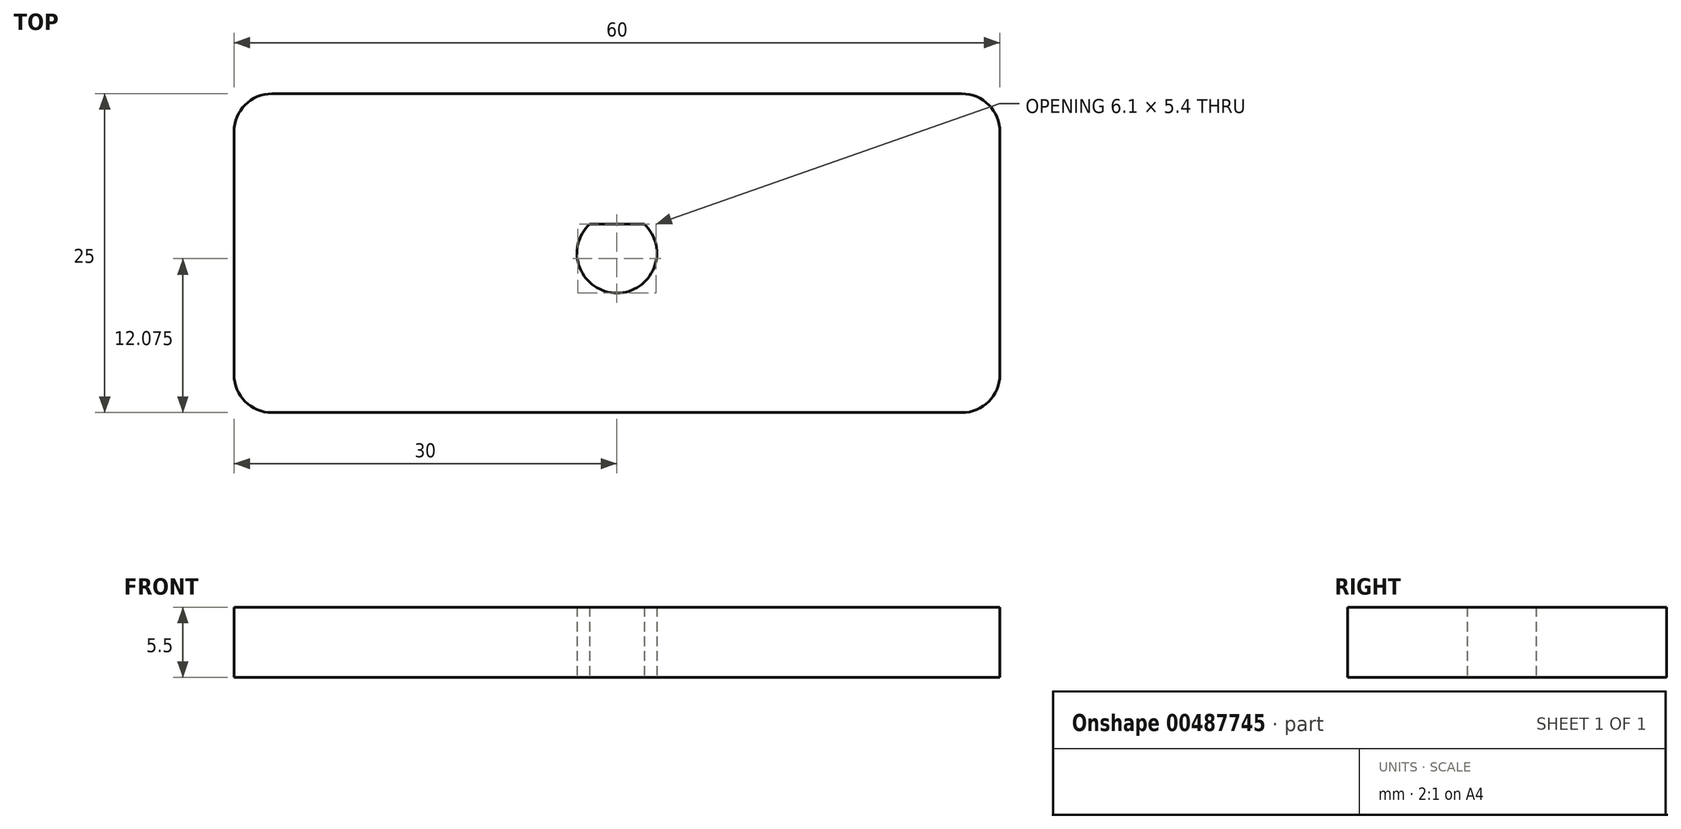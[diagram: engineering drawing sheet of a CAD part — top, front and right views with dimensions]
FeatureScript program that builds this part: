
annotation { "Feature Type Name" : "Feature", "Feature Type Description" : "" }
export const myFeature = defineFeature(function(context is Context, id is Id, definition is map)
    precondition{}
    {
        {
            var Q0;
            Q0=qCreatedBy(makeId("Top.planeOp"),FACE);
            var sketch = newSketch(context, id + "F0", { "sketchPlane" : qUnion([Q0])});
            skLineSegment(sketch, "E0.bottom", {"start": v(0, 0) * mm, "end": v(60, 0) * mm});
            skLineSegment(sketch, "E0.top", {"start": v(0, -25) * mm, "end": v(60, -25) * mm});
            skLineSegment(sketch, "E0.left", {"start": v(0, 0) * mm, "end": v(0, -25) * mm});
            skLineSegment(sketch, "E0.right", {"start": v(60, 0) * mm, "end": v(60, -25) * mm});
            skLineSegment(sketch, "E1", {"start": v(30, 0) * mm, "end": v(30, -25) * mm, "construction": true});
            skLineSegment(sketch, "E2", {"start": v(27.86, -10.22) * mm, "end": v(32.14, -10.22) * mm});
            skArc(sketch, "E3", {"start": v(27.86, -10.22) * mm, "mid": v(30, -15.62) * mm, "end": v(32.14, -10.22) * mm});
            skArc(sketch, "E4", {"start": v(32.14, -10.22) * mm, "mid": v(30, -9.38) * mm, "end": v(27.86, -10.22) * mm, "construction": true});
            skSolve(sketch);
        }
        {
            var Q0;
            Q0=makeQuery(id+"F0.imprint","IMPRINT",FACE,{"disambiguationData":[TD([[makeQuery(id+"F0.imprint","IMPRINT",EDGE,{"derivedFrom":sQuery(id+"F0.wireOp",EDGE,"E0.bottom")}),-1.0]])]});
            extrude(context, id + "F1", {"entities" : qUnion([Q0]), "depth" : 5.5 * mm});
        }
        {
            var Q0;
            Q0=makeQuery(id+"F1.opExtrude","SWEPT_EDGE",EDGE,{"disambiguationData":[OSD([sQuery(id+"F0.wireOp",EDGE,"E0.top"),sQuery(id+"F0.wireOp",EDGE,"E0.left")])]});
            var Q1;
            Q1=makeQuery(id+"F1.opExtrude","SWEPT_EDGE",EDGE,{"disambiguationData":[OSD([sQuery(id+"F0.wireOp",EDGE,"E0.top"),sQuery(id+"F0.wireOp",EDGE,"E0.right")])]});
            var Q2;
            Q2=makeQuery(id+"F1.opExtrude","SWEPT_EDGE",EDGE,{"disambiguationData":[OSD([sQuery(id+"F0.wireOp",EDGE,"E0.bottom"),sQuery(id+"F0.wireOp",EDGE,"E0.right")])]});
            var Q3;
            Q3=makeQuery(id+"F1.opExtrude","SWEPT_EDGE",EDGE,{"disambiguationData":[OSD([sQuery(id+"F0.wireOp",EDGE,"E0.bottom"),sQuery(id+"F0.wireOp",EDGE,"E0.left")])]});
            fillet(context, id + "F2", {"entities" : qUnion([Q0, Q1, Q2, Q3]), "radius" : 3 * mm, "tangentPropagation" : true, "allowEdgeOverflow" : false});
        }
    });
